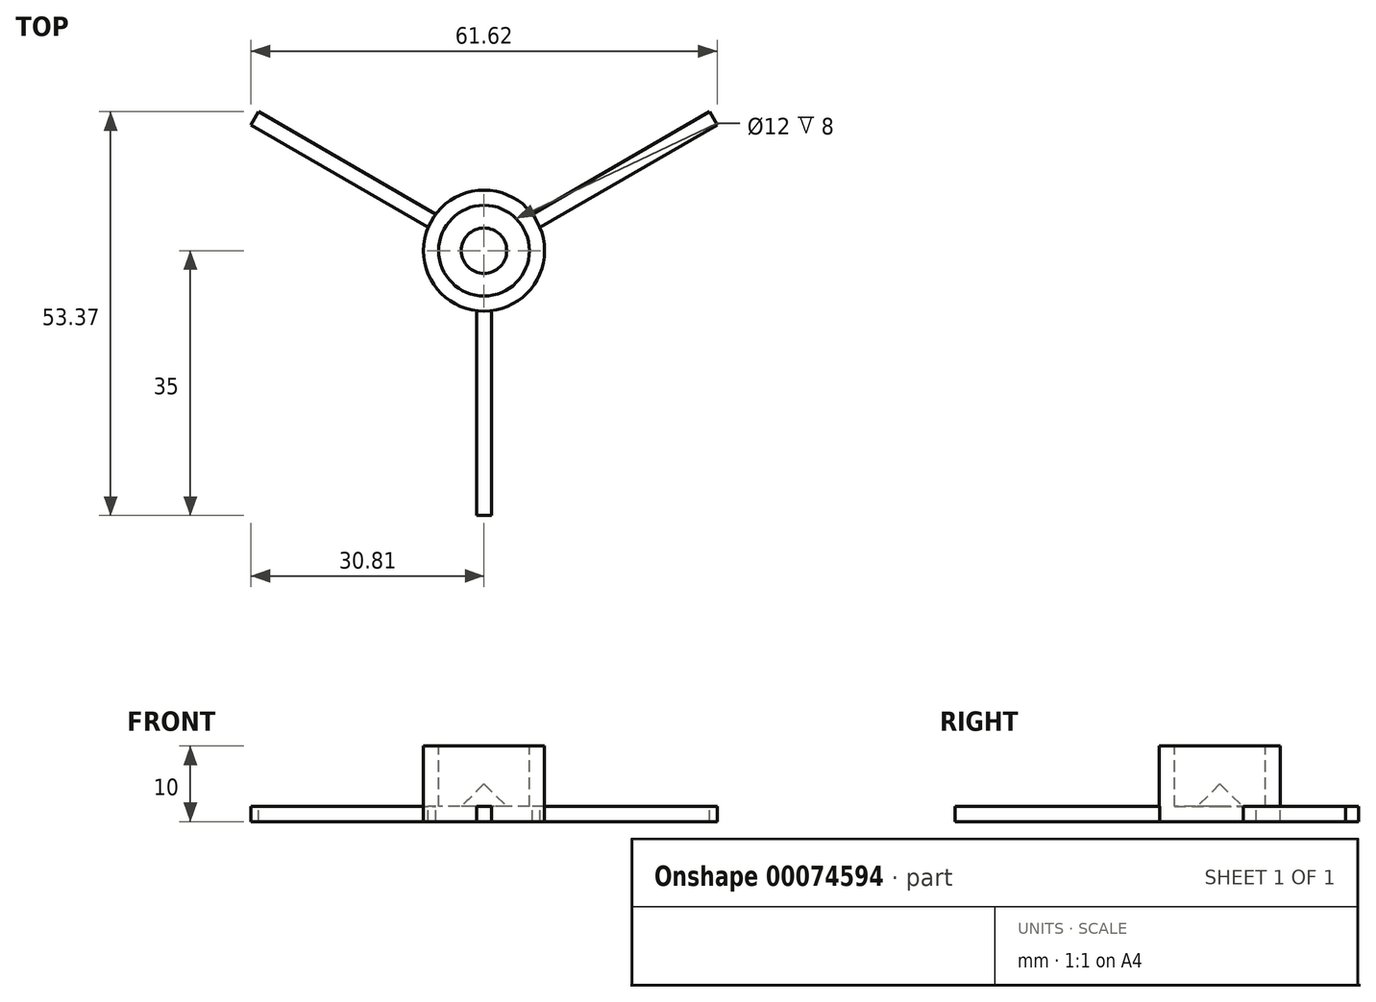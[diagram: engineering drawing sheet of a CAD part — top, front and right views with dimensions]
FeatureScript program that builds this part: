
annotation { "Feature Type Name" : "Feature", "Feature Type Description" : "" }
export const myFeature = defineFeature(function(context is Context, id is Id, definition is map)
    precondition{}
    {
        {
            var Q0;
            Q0=qCreatedBy(makeId("Front.planeOp"),FACE);
            var sketch = newSketch(context, id + "F0", { "sketchPlane" : qUnion([Q0])});
            skLineSegment(sketch, "E0", {"start": v(0, 0) * mm, "end": v(8, 0) * mm});
            skLineSegment(sketch, "E1", {"start": v(8, 0) * mm, "end": v(8, 10) * mm});
            skLineSegment(sketch, "E2", {"start": v(8, 10) * mm, "end": v(6, 10) * mm});
            skLineSegment(sketch, "E3", {"start": v(6, 10) * mm, "end": v(6, 2) * mm});
            skLineSegment(sketch, "E4", {"start": v(6, 2) * mm, "end": v(3, 2) * mm});
            skLineSegment(sketch, "E5", {"start": v(3, 2) * mm, "end": v(0, 5) * mm});
            skLineSegment(sketch, "E6", {"start": v(0, 5) * mm, "end": v(0, 0) * mm});
            skSolve(sketch);
        }
        {
            var Q0;
            Q0=makeQuery(id+"F0.imprint","IMPRINT",FACE,{"disambiguationData":[TD([[makeQuery(id+"F0.imprint","IMPRINT",EDGE,{"derivedFrom":sQuery(id+"F0.wireOp",EDGE,"E0")}),1.0]])]});
            var Q1;
            Q1=sQuery(id+"F0.wireOp",EDGE,"E6");
            revolve(context, id + "F2", {"entities" : qUnion([Q0]), "axis" : qUnion([Q1]), "revolveType" : RevolveType.FULL});
        }
        {
            var Q0;
            Q0=qCreatedBy(makeId("Front.planeOp"),FACE);
            var sketch = newSketch(context, id + "F3", { "sketchPlane" : qUnion([Q0])});
            skLineSegment(sketch, "E7.bottom", {"start": v(-1, 0) * mm, "end": v(1, 0) * mm});
            skLineSegment(sketch, "E7.top", {"start": v(-1, 2) * mm, "end": v(1, 2) * mm});
            skLineSegment(sketch, "E7.left", {"start": v(-1, 0) * mm, "end": v(-1, 2) * mm});
            skLineSegment(sketch, "E7.right", {"start": v(1, 0) * mm, "end": v(1, 2) * mm});
            skSolve(sketch);
        }
        {
            var Q0;
            Q0 = qSketchRegion(id + "F3", true);
            extrude(context, id + "F4", {"entities" : qUnion([Q0]), "operationType" : NewBodyOperationType.ADD, "depth" : 35 * mm});
        }
        {
            var Q0;
            Q0=makeQuery(id+"F2.opRevolve","SWEPT_BODY",BODY,{"disambiguationData":[OSD([sQuery(id+"F0.wireOp",EDGE,"E0"),sQuery(id+"F0.wireOp",EDGE,"E1"),sQuery(id+"F0.wireOp",EDGE,"E2"),sQuery(id+"F0.wireOp",EDGE,"E3"),sQuery(id+"F0.wireOp",EDGE,"E4"),sQuery(id+"F0.wireOp",EDGE,"E5"),sQuery(id+"F0.wireOp",EDGE,"E6")])]});
            var Q1;
            Q1=makeQuery(id+"F2.opRevolve","SWEPT_FACE",FACE,{"disambiguationData":[OSD([sQuery(id+"F0.wireOp",EDGE,"E5")])]});
            circularPattern(context, id + "F1", {"operationType" : NewBodyOperationType.ADD, "entities" : qUnion([Q0]), "axis" : qUnion([Q1]), "angle" : 360 * degree, "instanceCount" : 3, "equalSpace" : true});
        }
    });
